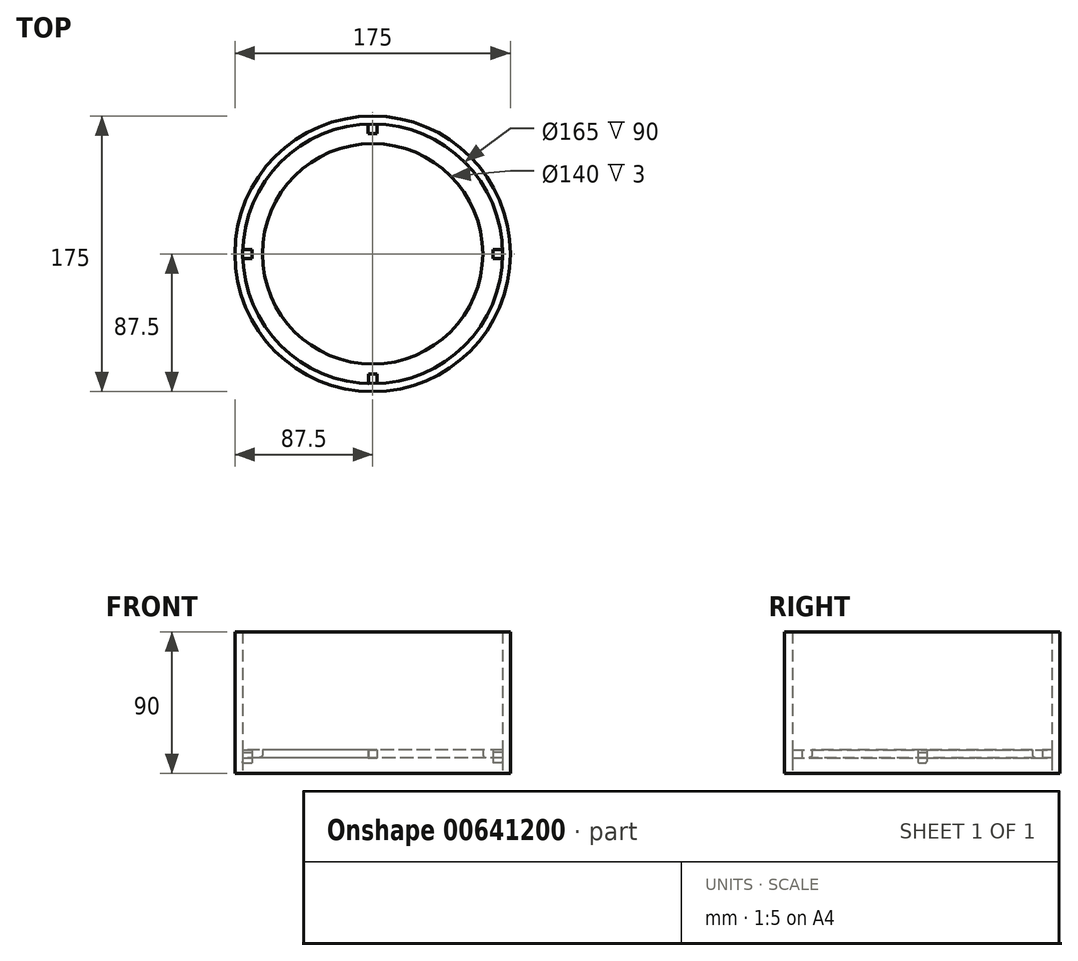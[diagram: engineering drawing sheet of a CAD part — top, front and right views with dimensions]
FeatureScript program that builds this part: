
annotation { "Feature Type Name" : "Feature", "Feature Type Description" : "" }
export const myFeature = defineFeature(function(context is Context, id is Id, definition is map)
    precondition{}
    {
        {
            var Q0;
            Q0=qCreatedBy(makeId("Top.planeOp"),FACE);
            var sketch = newSketch(context, id + "F0", { "sketchPlane" : qUnion([Q0])});
            skCircle(sketch, "E0", {"center": v(0, 0) * mm, "radius": 82.5 * mm});
            skCircle(sketch, "E1.0", {"center": v(0, 0) * mm, "radius": 87.5 * mm});
            skCircle(sketch, "E2", {"center": v(0, 0) * mm, "radius": 70 * mm});
            skLineSegment(sketch, "E3.bottom", {"start": v(2.87, -82.45) * mm, "end": v(-2.87, -82.45) * mm});
            skLineSegment(sketch, "E3.top", {"start": v(2.87, 82.45) * mm, "end": v(-2.87, 82.45) * mm});
            skLineSegment(sketch, "E4.1.2", {"start": v(-82.45, -2.87) * mm, "end": v(-82.45, 2.87) * mm});
            skLineSegment(sketch, "E4.1.3", {"start": v(82.45, -2.87) * mm, "end": v(82.45, 2.87) * mm});
            skLineSegment(sketch, "E5.bottom", {"start": v(82.45, 2.87) * mm, "end": v(76.45, 2.87) * mm});
            skLineSegment(sketch, "E5.top", {"start": v(82.45, -2.87) * mm, "end": v(76.45, -2.87) * mm});
            skLineSegment(sketch, "E5.left", {"start": v(82.45, 2.87) * mm, "end": v(82.45, -2.87) * mm});
            skLineSegment(sketch, "E5.right", {"start": v(76.45, 2.87) * mm, "end": v(76.45, -2.87) * mm});
            skLineSegment(sketch, "E6.bottom", {"start": v(-82.45, 2.87) * mm, "end": v(-76.45, 2.87) * mm});
            skLineSegment(sketch, "E6.top", {"start": v(-82.45, -2.87) * mm, "end": v(-76.45, -2.87) * mm});
            skLineSegment(sketch, "E6.left", {"start": v(-82.45, 2.87) * mm, "end": v(-82.45, -2.87) * mm});
            skLineSegment(sketch, "E6.right", {"start": v(-76.45, 2.87) * mm, "end": v(-76.45, -2.87) * mm});
            skLineSegment(sketch, "E7.bottom", {"start": v(2.87, -82.45) * mm, "end": v(-2.66, -82.45) * mm});
            skLineSegment(sketch, "E7.top", {"start": v(2.87, -76.45) * mm, "end": v(-2.66, -76.45) * mm});
            skLineSegment(sketch, "E7.left", {"start": v(2.87, -82.45) * mm, "end": v(2.87, -76.45) * mm});
            skLineSegment(sketch, "E7.right", {"start": v(-2.66, -82.45) * mm, "end": v(-2.66, -76.45) * mm});
            skLineSegment(sketch, "E8.bottom", {"start": v(-2.87, 82.45) * mm, "end": v(2.87, 82.45) * mm});
            skLineSegment(sketch, "E8.top", {"start": v(-2.87, 76.45) * mm, "end": v(2.87, 76.45) * mm});
            skLineSegment(sketch, "E8.left", {"start": v(-2.87, 82.45) * mm, "end": v(-2.87, 76.45) * mm});
            skLineSegment(sketch, "E8.right", {"start": v(2.87, 82.45) * mm, "end": v(2.87, 76.45) * mm});
            skSolve(sketch);
        }
        {
            var Q0;
            Q0 = qSketchRegion(id + "F0", true);
            extrude(context, id + "F1", {"entities" : qUnion([Q0]), "depth" : 90 * mm, "offsetDistance" : 25 * mm});
        }
        {
            var Q0;
            Q0=makeQuery(id+"F0.imprint","IMPRINT",FACE,{"disambiguationData":[TD([[makeQuery(id+"F0.imprint","IMPRINT",EDGE,{"derivedFrom":sQuery(id+"F0.wireOp",EDGE,"E0")}),1.0]])]});
            extrude(context, id + "F2", {"entities" : qUnion([Q0]), "operationType" : NewBodyOperationType.ADD, "depth" : 15 * mm, "offsetDistance" : 25 * mm, "hasSecondDirection" : true, "secondDirectionOppositeDirection" : false, "secondDirectionDepth" : 10 * mm});
        }
        {
            var Q0;
            Q0=makeQuery(id+"F0.imprint","IMPRINT",FACE,{"disambiguationData":[TD([[makeQuery(id+"F0.imprint","IMPRINT",EDGE,{"derivedFrom":sQuery(id+"F0.wireOp",EDGE,"E7.bottom")}),-1.0]])]});
            var Q1;
            Q1=makeQuery(id+"F0.imprint","IMPRINT",FACE,{"disambiguationData":[TD([[makeQuery(id+"F0.imprint","IMPRINT",EDGE,{"derivedFrom":sQuery(id+"F0.wireOp",EDGE,"E5.bottom")}),1.0]])]});
            var Q2;
            Q2=makeQuery(id+"F0.imprint","IMPRINT",FACE,{"disambiguationData":[TD([[makeQuery(id+"F0.imprint","IMPRINT",EDGE,{"derivedFrom":sQuery(id+"F0.wireOp",EDGE,"E8.bottom")}),-1.0]])]});
            var Q3;
            Q3=makeQuery(id+"F0.imprint","IMPRINT",FACE,{"disambiguationData":[TD([[makeQuery(id+"F0.imprint","IMPRINT",EDGE,{"derivedFrom":sQuery(id+"F0.wireOp",EDGE,"E6.bottom")}),-1.0]])]});
            extrude(context, id + "F3", {"entities" : qUnion([Q0, Q1, Q2, Q3]), "depth" : 13.4 * mm, "offsetDistance" : 25 * mm, "hasSecondDirection" : true, "secondDirectionOppositeDirection" : false, "secondDirectionDepth" : 6.7 * mm});
        }
        {
            var Q0;
            Q0=makeQuery(id+"F3.opExtrude","CAP_EDGE",EDGE,{"disambiguationData":[OSD([sQuery(id+"F0.wireOp",EDGE,"E7.right")])],"isStart":true});
            var Q1;
            Q1=makeQuery(id+"F3.opExtrude","CAP_EDGE",EDGE,{"disambiguationData":[OSD([sQuery(id+"F0.wireOp",EDGE,"E7.left")])],"isStart":true});
            var Q2;
            Q2=makeQuery(id+"F3.opExtrude","CAP_EDGE",EDGE,{"disambiguationData":[OSD([sQuery(id+"F0.wireOp",EDGE,"E5.bottom")])],"isStart":true});
            var Q3;
            Q3=makeQuery(id+"F3.opExtrude","CAP_EDGE",EDGE,{"disambiguationData":[OSD([sQuery(id+"F0.wireOp",EDGE,"E5.top")])],"isStart":true});
            var Q4;
            Q4=makeQuery(id+"F3.opExtrude","CAP_EDGE",EDGE,{"disambiguationData":[OSD([sQuery(id+"F0.wireOp",EDGE,"E8.right")])],"isStart":true});
            var Q5;
            Q5=makeQuery(id+"F3.opExtrude","CAP_EDGE",EDGE,{"disambiguationData":[OSD([sQuery(id+"F0.wireOp",EDGE,"E8.left")])],"isStart":true});
            var Q6;
            Q6=makeQuery(id+"F3.opExtrude","CAP_EDGE",EDGE,{"disambiguationData":[OSD([sQuery(id+"F0.wireOp",EDGE,"E6.bottom")])],"isStart":true});
            var Q7;
            Q7=makeQuery(id+"F3.opExtrude","CAP_EDGE",EDGE,{"disambiguationData":[OSD([sQuery(id+"F0.wireOp",EDGE,"E6.top")])],"isStart":true});
            fillet(context, id + "F4", {"entities" : qUnion([Q0, Q1, Q2, Q3, Q4, Q5, Q6, Q7]), "radius" : 1 * mm, "tangentPropagation" : true, "allowEdgeOverflow" : false});
        }
        {
            var Q0;
            Q0=makeQuery(id+"F2.opExtrude","CAP_EDGE",EDGE,{"disambiguationData":[OSD([sQuery(id+"F0.wireOp",EDGE,"E2")])],"isStart":true});
            fillet(context, id + "F5", {"entities" : qUnion([Q0]), "radius" : 2 * mm, "tangentPropagation" : true, "allowEdgeOverflow" : false});
        }
    });
